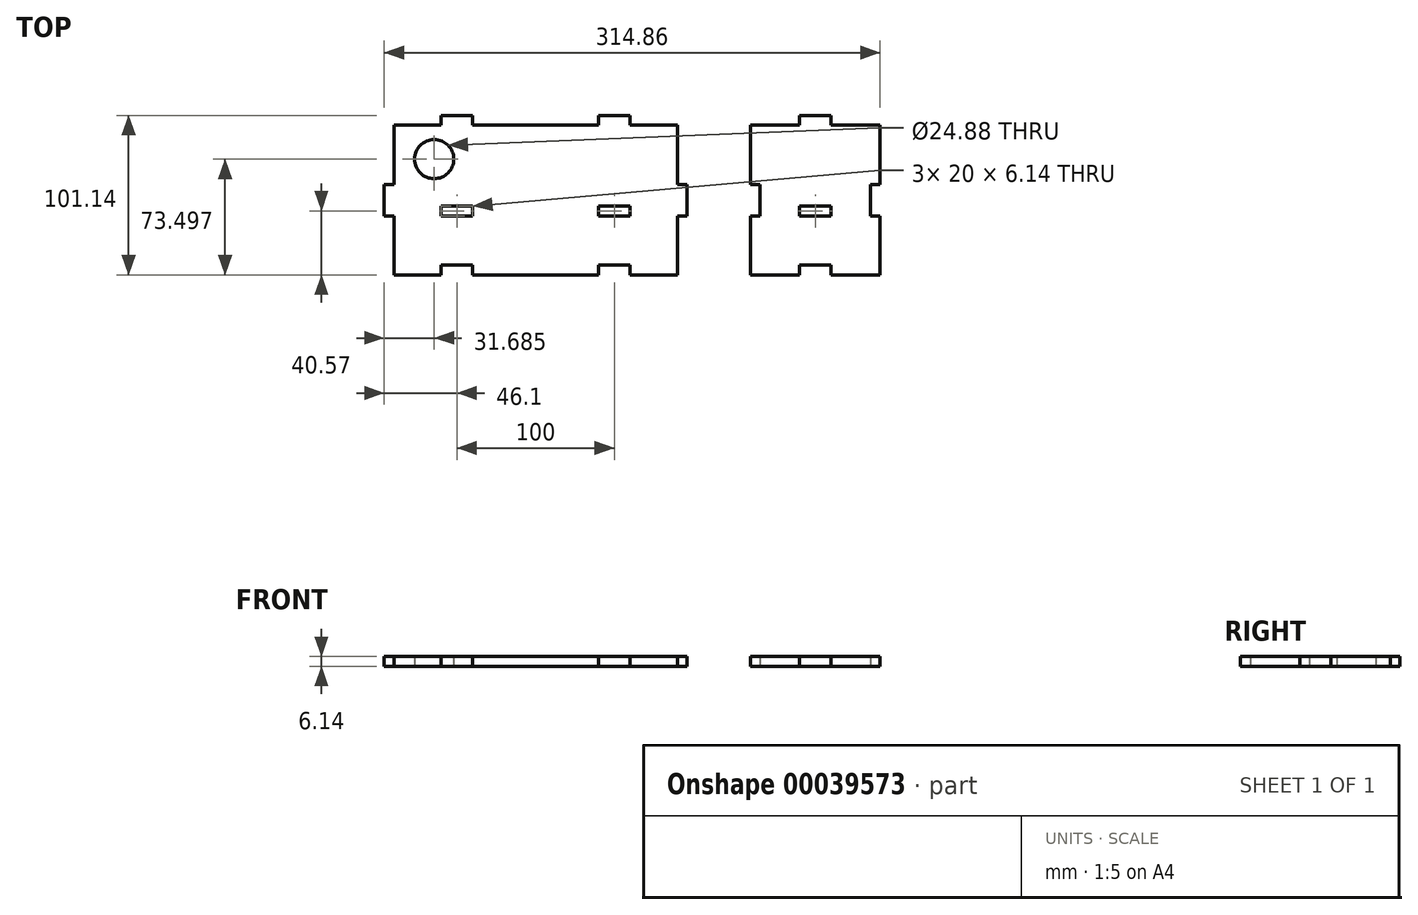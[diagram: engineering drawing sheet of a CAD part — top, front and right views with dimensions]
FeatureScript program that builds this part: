
annotation { "Feature Type Name" : "Feature", "Feature Type Description" : "" }
export const myFeature = defineFeature(function(context is Context, id is Id, definition is map)
    precondition{}
    {
        {
            assignVariable(context, id + "F0", {"name" : "PanelThickness", "anyValue" : 6.14});
        }
        {
            var Q0;
            Q0=qCreatedBy(makeId("Top.planeOp"),FACE);
            var sketch = newSketch(context, id + "F1", { "sketchPlane" : qUnion([Q0])});
            skPoint(sketch, "E0.0", {"position": v(-90, 47.5) * mm});
            skLineSegment(sketch, "E1", {"start": v(-90, -47.5) * mm, "end": v(-60, -47.5) * mm});
            skLineSegment(sketch, "E2", {"start": v(-40, -47.5) * mm, "end": v(40, -47.5) * mm});
            skLineSegment(sketch, "E3", {"start": v(40, -41.36) * mm, "end": v(60, -41.36) * mm});
            skLineSegment(sketch, "E4", {"start": v(60, -47.5) * mm, "end": v(90, -47.5) * mm});
            skLineSegment(sketch, "E5", {"start": v(90, 47.5) * mm, "end": v(90, -10) * mm});
            skLineSegment(sketch, "E6", {"start": v(-90, -47.5) * mm, "end": v(-90, 47.5) * mm});
            skLineSegment(sketch, "E7", {"start": v(-90, 47.5) * mm, "end": v(-60, 47.5) * mm});
            skLineSegment(sketch, "E8", {"start": v(-60, 53.64) * mm, "end": v(-40, 53.64) * mm});
            skLineSegment(sketch, "E9", {"start": v(40, 53.64) * mm, "end": v(60, 53.64) * mm});
            skLineSegment(sketch, "E10", {"start": v(60, 47.5) * mm, "end": v(90, 47.5) * mm});
            skLineSegment(sketch, "E11", {"start": v(-40, 47.5) * mm, "end": v(40, 47.5) * mm});
            skLineSegment(sketch, "E12", {"start": v(60, 47.5) * mm, "end": v(60, 53.64) * mm});
            skLineSegment(sketch, "E13", {"start": v(40, 47.5) * mm, "end": v(40, 53.64) * mm});
            skLineSegment(sketch, "E14", {"start": v(-40, 47.5) * mm, "end": v(-40, 53.64) * mm});
            skLineSegment(sketch, "E15", {"start": v(-60, 47.5) * mm, "end": v(-60, 53.64) * mm});
            skLineSegment(sketch, "E16", {"start": v(40, -47.5) * mm, "end": v(40, -41.36) * mm});
            skLineSegment(sketch, "E17", {"start": v(60, -47.5) * mm, "end": v(60, -41.36) * mm});
            skLineSegment(sketch, "E18", {"start": v(-60, -41.36) * mm, "end": v(-40, -41.36) * mm});
            skLineSegment(sketch, "E19", {"start": v(-40, -47.5) * mm, "end": v(-40, -41.36) * mm});
            skLineSegment(sketch, "E20", {"start": v(-60, -47.5) * mm, "end": v(-60, -41.36) * mm});
            skLineSegment(sketch, "E21.top", {"start": v(90, 10) * mm, "end": v(96.1, 10) * mm});
            skLineSegment(sketch, "E22.top", {"start": v(90, -10) * mm, "end": v(96.1, -10) * mm});
            skLineSegment(sketch, "E23", {"start": v(0, -47.5) * mm, "end": v(0, 47.5) * mm, "construction": true});
            skLineSegment(sketch, "E24.0", {"start": v(-60, -3.86) * mm, "end": v(-60, -10) * mm});
            skLineSegment(sketch, "E24.1", {"start": v(-40, -3.86) * mm, "end": v(-60, -3.86) * mm});
            skLineSegment(sketch, "E24.2", {"start": v(-40, -3.86) * mm, "end": v(-40, -10) * mm});
            skLineSegment(sketch, "E24.3", {"start": v(-40, -10) * mm, "end": v(-60, -10) * mm});
            skLineSegment(sketch, "E24.4", {"start": v(40, -3.86) * mm, "end": v(40, -10) * mm});
            skLineSegment(sketch, "E24.5", {"start": v(40, -3.86) * mm, "end": v(60, -3.86) * mm});
            skLineSegment(sketch, "E24.6", {"start": v(40, -10) * mm, "end": v(60, -10) * mm});
            skLineSegment(sketch, "E24.7", {"start": v(60, -3.86) * mm, "end": v(60, -10) * mm});
            skLineSegment(sketch, "E25", {"start": v(90, -10) * mm, "end": v(90, -47.5) * mm});
            skLineSegment(sketch, "E26.0", {"start": v(96.1, 166.39) * mm, "end": v(96.1, 84.1) * mm, "construction": true});
            skLineSegment(sketch, "E27.0", {"start": v(96.1, 166.39) * mm, "end": v(-96.18, 166.39) * mm, "construction": true});
            skPoint(sketch, "E28.rect.middle", {"position": v(-0.04, 125.25) * mm});
            skLineSegment(sketch, "E29.MirrorCS", {"start": v(39.96, 166.39) * mm, "end": v(59.96, 166.39) * mm});
            skLineSegment(sketch, "E28.rect.bottom", {"start": v(89.96, 160.25) * mm, "end": v(-90.04, 160.25) * mm});
            skLineSegment(sketch, "E28.rect.top", {"start": v(89.96, 90.25) * mm, "end": v(-90.04, 90.25) * mm});
            skLineSegment(sketch, "E28.rect.left", {"start": v(89.96, 160.25) * mm, "end": v(89.96, 90.25) * mm});
            skLineSegment(sketch, "E28.rect.right", {"start": v(-90.04, 160.25) * mm, "end": v(-90.04, 90.25) * mm});
            skLineSegment(sketch, "E30.bottom", {"start": v(40, 90.25) * mm, "end": v(60, 90.25) * mm});
            skLineSegment(sketch, "E30.top", {"start": v(40, 84.1) * mm, "end": v(60, 84.1) * mm});
            skLineSegment(sketch, "E31.MirrorCS", {"start": v(-40, 84.1) * mm, "end": v(-60, 84.1) * mm});
            skLineSegment(sketch, "E32.MirrorCS", {"start": v(-40.04, 166.39) * mm, "end": v(-60.04, 166.39) * mm});
            skLineSegment(sketch, "E33.0", {"start": v(96.1, 84.1) * mm, "end": v(-96.18, 84.1) * mm, "construction": true});
            skLineSegment(sketch, "E34.0", {"start": v(-96.18, 166.39) * mm, "end": v(-96.18, 84.1) * mm, "construction": true});
            skLineSegment(sketch, "E35.MirrorCS", {"start": v(96.1, 115.25) * mm, "end": v(96.1, 135.25) * mm});
            skLineSegment(sketch, "E36.right", {"start": v(-96.18, 115.25) * mm, "end": v(-96.18, 135.25) * mm});
            skPoint(sketch, "E37", {"position": v(-96.18, 125.25) * mm});
            skLineSegment(sketch, "E38.MirrorCS", {"start": v(89.96, 115.25) * mm, "end": v(96.1, 115.25) * mm});
            skLineSegment(sketch, "E36.left", {"start": v(-90.04, 115.25) * mm, "end": v(-90.04, 135.25) * mm});
            skLineSegment(sketch, "E39.MirrorCS", {"start": v(-60.04, 160.25) * mm, "end": v(-60.04, 166.39) * mm});
            skLineSegment(sketch, "E40.MirrorCS", {"start": v(39.96, 160.25) * mm, "end": v(39.96, 166.39) * mm});
            skLineSegment(sketch, "E41.MirrorCS", {"start": v(-40, 90.25) * mm, "end": v(-40, 84.1) * mm});
            skLineSegment(sketch, "E42.MirrorCS", {"start": v(-60, 90.25) * mm, "end": v(-60, 84.1) * mm});
            skLineSegment(sketch, "E43.MirrorCS", {"start": v(-40.04, 160.25) * mm, "end": v(-40.04, 166.39) * mm});
            skLineSegment(sketch, "E44.MirrorCS", {"start": v(89.96, 135.25) * mm, "end": v(96.1, 135.25) * mm});
            skLineSegment(sketch, "E45.MirrorCS", {"start": v(59.96, 160.25) * mm, "end": v(59.96, 166.39) * mm});
            skLineSegment(sketch, "E36.bottom", {"start": v(-90.04, 115.25) * mm, "end": v(-96.18, 115.25) * mm});
            skLineSegment(sketch, "E30.left", {"start": v(40, 90.25) * mm, "end": v(40, 84.1) * mm});
            skLineSegment(sketch, "E30.right", {"start": v(60, 90.25) * mm, "end": v(60, 84.1) * mm});
            skLineSegment(sketch, "E36.top", {"start": v(-90.04, 135.25) * mm, "end": v(-96.18, 135.25) * mm});
            skLineSegment(sketch, "E46", {"start": v(-60, 53.64) * mm, "end": v(-60, -67.68) * mm, "construction": true});
            skLineSegment(sketch, "E47", {"start": v(-40, 53.64) * mm, "end": v(-40, -72.3) * mm, "construction": true});
            skLineSegment(sketch, "E48", {"start": v(40, 47.5) * mm, "end": v(40, -61.26) * mm, "construction": true});
            skLineSegment(sketch, "E49", {"start": v(60, 47.5) * mm, "end": v(60, -68.98) * mm, "construction": true});
            skLineSegment(sketch, "E50.right", {"start": v(212.62, -10) * mm, "end": v(212.62, 10) * mm});
            skLineSegment(sketch, "E51", {"start": v(167.62, -41.36) * mm, "end": v(187.62, -41.36) * mm});
            skLineSegment(sketch, "E52", {"start": v(136.48, -47.5) * mm, "end": v(136.48, -10) * mm});
            skLineSegment(sketch, "E53", {"start": v(136.48, 47.5) * mm, "end": v(167.62, 47.5) * mm});
            skLineSegment(sketch, "E54", {"start": v(167.62, 53.64) * mm, "end": v(187.62, 53.64) * mm});
            skLineSegment(sketch, "E55", {"start": v(187.62, 47.5) * mm, "end": v(218.76, 47.5) * mm});
            skLineSegment(sketch, "E56", {"start": v(136.48, -10) * mm, "end": v(212.62, -10) * mm, "construction": true});
            skLineSegment(sketch, "E57", {"start": v(136.48, 10) * mm, "end": v(212.62, 10) * mm, "construction": true});
            skPoint(sketch, "E58.rect.middle", {"position": v(177.62, -6.93) * mm});
            skLineSegment(sketch, "E59", {"start": v(218.76, -47.5) * mm, "end": v(218.76, -10) * mm});
            skLineSegment(sketch, "E60.0", {"start": v(142.62, -10) * mm, "end": v(142.62, 10) * mm});
            skLineSegment(sketch, "E61", {"start": v(167.62, -41.36) * mm, "end": v(167.62, 47.5) * mm, "construction": true});
            skLineSegment(sketch, "E62", {"start": v(187.62, -41.36) * mm, "end": v(187.62, 47.5) * mm, "construction": true});
            skLineSegment(sketch, "E58.rect.bottom", {"start": v(187.62, -10) * mm, "end": v(167.62, -10) * mm});
            skLineSegment(sketch, "E58.rect.top", {"start": v(187.62, -3.86) * mm, "end": v(167.62, -3.86) * mm});
            skLineSegment(sketch, "E50.bottom", {"start": v(218.76, -10) * mm, "end": v(212.62, -10) * mm});
            skLineSegment(sketch, "E58.rect.left", {"start": v(187.62, -10) * mm, "end": v(187.62, -3.86) * mm});
            skLineSegment(sketch, "E58.rect.right", {"start": v(167.62, -10) * mm, "end": v(167.62, -3.86) * mm});
            skLineSegment(sketch, "E50.top", {"start": v(218.76, 10) * mm, "end": v(212.62, 10) * mm});
            skLineSegment(sketch, "E63.bottom", {"start": v(136.48, -10) * mm, "end": v(142.62, -10) * mm});
            skLineSegment(sketch, "E64", {"start": v(167.62, 53.64) * mm, "end": v(167.62, 47.5) * mm});
            skLineSegment(sketch, "E65", {"start": v(187.62, 53.64) * mm, "end": v(187.62, 47.5) * mm});
            skLineSegment(sketch, "E66", {"start": v(90, 47.5) * mm, "end": v(136.48, 47.5) * mm, "construction": true});
            skLineSegment(sketch, "E67", {"start": v(90, -47.5) * mm, "end": v(136.48, -47.5) * mm, "construction": true});
            skLineSegment(sketch, "E68", {"start": v(136.48, -10) * mm, "end": v(96.1, -10) * mm, "construction": true});
            skLineSegment(sketch, "E69", {"start": v(96.1, -10) * mm, "end": v(96.1, 10) * mm});
            skLineSegment(sketch, "E70", {"start": v(-96.1, 0) * mm, "end": v(244.4, 0) * mm, "construction": true});
            skLineSegment(sketch, "E71", {"start": v(167.62, -41.36) * mm, "end": v(167.62, -47.5) * mm});
            skLineSegment(sketch, "E72", {"start": v(167.62, -47.5) * mm, "end": v(136.48, -47.5) * mm});
            skLineSegment(sketch, "E73", {"start": v(187.62, -41.36) * mm, "end": v(187.62, -47.5) * mm});
            skLineSegment(sketch, "E74", {"start": v(187.62, -47.5) * mm, "end": v(218.76, -47.5) * mm});
            skLineSegment(sketch, "E75", {"start": v(-60, 53.64) * mm, "end": v(-60, 84.1) * mm, "construction": true});
            skLineSegment(sketch, "E76", {"start": v(136.48, 10) * mm, "end": v(136.48, 47.5) * mm});
            skLineSegment(sketch, "E77", {"start": v(218.76, 10) * mm, "end": v(218.76, 47.5) * mm});
            skLineSegment(sketch, "E78", {"start": v(90, -10) * mm, "end": v(-131.67, -10) * mm, "construction": true});
            skLineSegment(sketch, "E79", {"start": v(136.48, 10) * mm, "end": v(-134.87, 10) * mm, "construction": true});
            skLineSegment(sketch, "E80", {"start": v(-96.1, 10) * mm, "end": v(-90, 10) * mm});
            skLineSegment(sketch, "E81", {"start": v(-90, -10) * mm, "end": v(-96.1, -10) * mm});
            skLineSegment(sketch, "E82", {"start": v(-96.1, 10) * mm, "end": v(-96.1, -10) * mm});
            skLineSegment(sketch, "E83", {"start": v(136.48, 10) * mm, "end": v(142.62, 10) * mm});
            skCircle(sketch, "E84", {"center": v(-64.41, 26) * mm, "radius": 12.44 * mm});
            skPoint(sketch, "E85", {"position": v(-90, 0) * mm});
            skPoint(sketch, "E86", {"position": v(-96.1, 0) * mm});
            skLineSegment(sketch, "E87", {"start": v(-40, 53.64) * mm, "end": v(40, 53.64) * mm, "construction": true});
            skLineSegment(sketch, "E88", {"start": v(60, 53.64) * mm, "end": v(167.62, 53.64) * mm, "construction": true});
            skLineSegment(sketch, "E89", {"start": v(-40, -41.36) * mm, "end": v(40, -41.36) * mm, "construction": true});
            skLineSegment(sketch, "E90", {"start": v(60, -41.36) * mm, "end": v(167.62, -41.36) * mm, "construction": true});
            skLineSegment(sketch, "E91", {"start": v(142.62, -6.93) * mm, "end": v(212.62, -6.93) * mm, "construction": true});
            skSolve(sketch);
        }
        {
            var Q0;
            {var subQ1=sQuery(id+"F1.wireOp",EDGE,"E1");Q0=makeQuery(id+"F1.imprint","IMPRINT",FACE,{"disambiguationData":[TD([[makeQuery(id+"F1.imprint","IMPRINT",EDGE,{"derivedFrom":subQ1}),1.0]])]});}
            var Q1;
            {var subQ4=sQuery(id+"F1.wireOp",EDGE,"3b86b983-0263-44d0-8503-49f76be5f0d3.MirrorCS");Q1=makeQuery(id+"F1.imprint","IMPRINT",FACE,{"disambiguationData":[TD([[makeQuery(id+"F1.imprint","IMPRINT",EDGE,{"derivedFrom":subQ4}),-1.0]])]});}
            var Q2;
            {var subQ4=sQuery(id+"F1.wireOp",EDGE,"E22.bottom");Q2=makeQuery(id+"F1.imprint","IMPRINT",FACE,{"disambiguationData":[TD([[makeQuery(id+"F1.imprint","IMPRINT",EDGE,{"derivedFrom":subQ4}),-1.0]])]});}
            var Q3;
            Q3=makeQuery(id+"F1.imprint","IMPRINT",FACE,{"disambiguationData":[TD([[makeQuery(id+"F1.imprint","IMPRINT",EDGE,{"derivedFrom":sQuery(id+"F1.wireOp",EDGE,"E21.top")}),-1.0]])]});
            var Q4;
            {var subQ1=sQuery(id+"F1.wireOp",EDGE,"E80");Q4=makeQuery(id+"F1.imprint","IMPRINT",FACE,{"disambiguationData":[TD([[makeQuery(id+"F1.imprint","IMPRINT",EDGE,{"derivedFrom":subQ1}),-1.0]])]});}
            extrude(context, id + "F2", {"entities" : qUnion([Q0, Q1, Q2, Q3, Q4]), "depth" : (getVariable(context, 'PanelThickness')) * mm});
        }
        {
            var Q0;
            Q0=makeQuery(id+"F1.imprint","IMPRINT",FACE,{"disambiguationData":[TD([[makeQuery(id+"F1.imprint","IMPRINT",EDGE,{"derivedFrom":sQuery(id+"F1.wireOp",EDGE,"E50.right")}),1.0]])]});
            extrude(context, id + "F3", {"entities" : qUnion([Q0]), "depth" : (getVariable(context, 'PanelThickness')) * mm});
        }
    });
